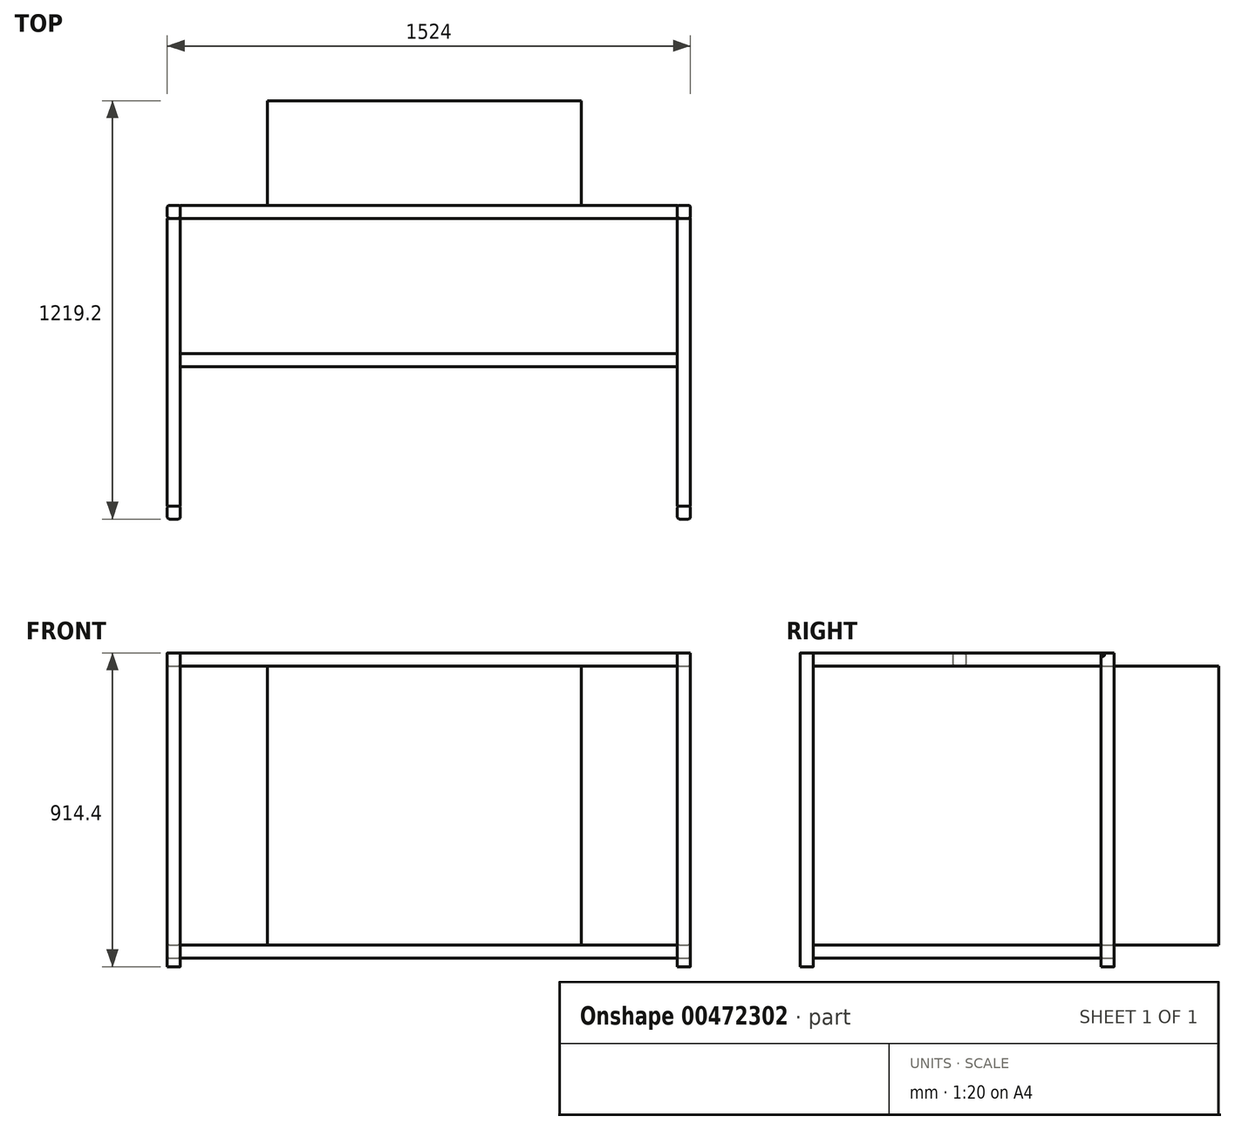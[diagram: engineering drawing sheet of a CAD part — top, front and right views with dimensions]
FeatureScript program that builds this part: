
annotation { "Feature Type Name" : "Feature", "Feature Type Description" : "" }
export const myFeature = defineFeature(function(context is Context, id is Id, definition is map)
    precondition{}
    {
        {
            var Q0;
            Q0=qCreatedBy(makeId("Top.planeOp"),FACE);
            var sketch = newSketch(context, id + "F0", { "sketchPlane" : qUnion([Q0])});
            skLineSegment(sketch, "E0.bottom", {"start": v(-762, 731.56) * mm, "end": v(-723.9, 731.56) * mm});
            skLineSegment(sketch, "E0.top", {"start": v(-762, 693.46) * mm, "end": v(-723.9, 693.46) * mm});
            skLineSegment(sketch, "E0.left", {"start": v(-762, 731.56) * mm, "end": v(-762, 693.46) * mm});
            skLineSegment(sketch, "E0.right", {"start": v(-723.9, 731.56) * mm, "end": v(-723.9, 693.46) * mm});
            skLineSegment(sketch, "E1.bottom", {"start": v(-762, -144.74) * mm, "end": v(-723.9, -144.74) * mm});
            skLineSegment(sketch, "E1.top", {"start": v(-762, -182.84) * mm, "end": v(-723.9, -182.84) * mm});
            skLineSegment(sketch, "E1.left", {"start": v(-762, -144.74) * mm, "end": v(-762, -182.84) * mm});
            skLineSegment(sketch, "E1.right", {"start": v(-723.9, -144.74) * mm, "end": v(-723.9, -182.84) * mm});
            skLineSegment(sketch, "E2.bottom", {"start": v(723.9, -182.84) * mm, "end": v(762, -182.84) * mm});
            skLineSegment(sketch, "E2.top", {"start": v(723.9, -144.74) * mm, "end": v(762, -144.74) * mm});
            skLineSegment(sketch, "E2.left", {"start": v(723.9, -182.84) * mm, "end": v(723.9, -144.74) * mm});
            skLineSegment(sketch, "E2.right", {"start": v(762, -182.84) * mm, "end": v(762, -144.74) * mm});
            skLineSegment(sketch, "E3.bottom", {"start": v(723.9, 731.56) * mm, "end": v(762, 731.56) * mm});
            skLineSegment(sketch, "E3.top", {"start": v(723.9, 693.46) * mm, "end": v(762, 693.46) * mm});
            skLineSegment(sketch, "E3.left", {"start": v(723.9, 731.56) * mm, "end": v(723.9, 693.46) * mm});
            skLineSegment(sketch, "E3.right", {"start": v(762, 731.56) * mm, "end": v(762, 693.46) * mm});
            skSolve(sketch);
        }
        {
            var Q0;
            Q0 = qSketchRegion(id + "F0", true);
            extrude(context, id + "F1", {"entities" : qUnion([Q0]), "depth" : 914.4 * mm});
        }
        {
            var Q0;
            Q0=makeQuery(id+"F1.opExtrude","SWEPT_EDGE",EDGE,{"disambiguationData":[OSD([sQuery(id+"F0.wireOp",EDGE,"E1.top"),sQuery(id+"F0.wireOp",EDGE,"E1.left")])]});
            var Q1;
            Q1=makeQuery(id+"F1.opExtrude","SWEPT_EDGE",EDGE,{"disambiguationData":[OSD([sQuery(id+"F0.wireOp",EDGE,"E1.top"),sQuery(id+"F0.wireOp",EDGE,"E1.right")])]});
            var Q2;
            Q2=makeQuery(id+"F1.opExtrude","SWEPT_EDGE",EDGE,{"disambiguationData":[OSD([sQuery(id+"F0.wireOp",EDGE,"E1.bottom"),sQuery(id+"F0.wireOp",EDGE,"E1.right")])]});
            var Q3;
            Q3=makeQuery(id+"F1.opExtrude","SWEPT_EDGE",EDGE,{"disambiguationData":[OSD([sQuery(id+"F0.wireOp",EDGE,"E0.top"),sQuery(id+"F0.wireOp",EDGE,"E0.left")])]});
            var Q4;
            Q4=makeQuery(id+"F1.opExtrude","SWEPT_EDGE",EDGE,{"disambiguationData":[OSD([sQuery(id+"F0.wireOp",EDGE,"E0.top"),sQuery(id+"F0.wireOp",EDGE,"E0.right")])]});
            var Q5;
            Q5=makeQuery(id+"F1.opExtrude","SWEPT_EDGE",EDGE,{"disambiguationData":[OSD([sQuery(id+"F0.wireOp",EDGE,"E0.bottom"),sQuery(id+"F0.wireOp",EDGE,"E0.right")])]});
            var Q6;
            Q6=makeQuery(id+"F1.opExtrude","SWEPT_EDGE",EDGE,{"disambiguationData":[OSD([sQuery(id+"F0.wireOp",EDGE,"E2.bottom"),sQuery(id+"F0.wireOp",EDGE,"E2.left")])]});
            var Q7;
            Q7=makeQuery(id+"F1.opExtrude","SWEPT_EDGE",EDGE,{"disambiguationData":[OSD([sQuery(id+"F0.wireOp",EDGE,"E2.bottom"),sQuery(id+"F0.wireOp",EDGE,"E2.right")])]});
            var Q8;
            Q8=makeQuery(id+"F1.opExtrude","SWEPT_EDGE",EDGE,{"disambiguationData":[OSD([sQuery(id+"F0.wireOp",EDGE,"E2.top"),sQuery(id+"F0.wireOp",EDGE,"E2.right")])]});
            var Q9;
            Q9=makeQuery(id+"F1.opExtrude","SWEPT_EDGE",EDGE,{"disambiguationData":[OSD([sQuery(id+"F0.wireOp",EDGE,"E3.top"),sQuery(id+"F0.wireOp",EDGE,"E3.left")])]});
            var Q10;
            Q10=makeQuery(id+"F1.opExtrude","SWEPT_EDGE",EDGE,{"disambiguationData":[OSD([sQuery(id+"F0.wireOp",EDGE,"E3.top"),sQuery(id+"F0.wireOp",EDGE,"E3.right")])]});
            var Q11;
            Q11=makeQuery(id+"F1.opExtrude","SWEPT_EDGE",EDGE,{"disambiguationData":[OSD([sQuery(id+"F0.wireOp",EDGE,"E3.bottom"),sQuery(id+"F0.wireOp",EDGE,"E3.right")])]});
            var Q12;
            Q12=makeQuery(id+"F1.opExtrude","SWEPT_EDGE",EDGE,{"disambiguationData":[OSD([sQuery(id+"F0.wireOp",EDGE,"E1.bottom"),sQuery(id+"F0.wireOp",EDGE,"E1.left")])]});
            var Q13;
            Q13=makeQuery(id+"F1.opExtrude","SWEPT_EDGE",EDGE,{"disambiguationData":[OSD([sQuery(id+"F0.wireOp",EDGE,"E2.top"),sQuery(id+"F0.wireOp",EDGE,"E2.left")])]});
            var Q14;
            Q14=makeQuery(id+"F1.opExtrude","SWEPT_EDGE",EDGE,{"disambiguationData":[OSD([sQuery(id+"F0.wireOp",EDGE,"E3.bottom"),sQuery(id+"F0.wireOp",EDGE,"E3.left")])]});
            var Q15;
            Q15=makeQuery(id+"F1.opExtrude","SWEPT_EDGE",EDGE,{"disambiguationData":[OSD([sQuery(id+"F0.wireOp",EDGE,"E0.bottom"),sQuery(id+"F0.wireOp",EDGE,"E0.left")])]});
            fillet(context, id + "F2", {"entities" : qUnion([Q0, Q1, Q2, Q3, Q4, Q5, Q6, Q7, Q8, Q9, Q10, Q11, Q12, Q13, Q14, Q15]), "radius" : 6.35 * mm, "tangentPropagation" : true, "allowEdgeOverflow" : false});
        }
        {
            var Q0;
            Q0=makeQuery(id+"F1.opExtrude","SWEPT_FACE",FACE,{"disambiguationData":[OSD([sQuery(id+"F0.wireOp",EDGE,"E3.right")])]});
            var sketch = newSketch(context, id + "F3", { "sketchPlane" : qUnion([Q0])});
            skLineSegment(sketch, "E4.bottom", {"start": v(-144.74, 914.4) * mm, "end": v(693.46, 914.4) * mm});
            skLineSegment(sketch, "E4.top", {"start": v(-144.74, 876.3) * mm, "end": v(693.46, 876.3) * mm});
            skLineSegment(sketch, "E4.left", {"start": v(-144.74, 914.4) * mm, "end": v(-144.74, 876.3) * mm});
            skLineSegment(sketch, "E4.right", {"start": v(693.46, 914.4) * mm, "end": v(693.46, 876.3) * mm});
            skSolve(sketch);
        }
        {
            var Q0;
            Q0=makeQuery(id+"F3.imprint","IMPRINT",FACE,{"disambiguationData":[TD([[makeQuery(id+"F3.imprint","IMPRINT",EDGE,{"derivedFrom":sQuery(id+"F3.wireOp",EDGE,"E4.bottom")}),-1.0]])]});
            extrude(context, id + "F4", {"entities" : qUnion([Q0]), "oppositeDirection" : true, "depth" : 38.1 * mm});
        }
        {
            var Q0;
            Q0=makeQuery(id+"F4.opExtrude","CAP_EDGE",EDGE,{"disambiguationData":[OSD([sQuery(id+"F3.wireOp",EDGE,"E4.bottom")])],"isStart":true});
            var Q1;
            Q1=makeQuery(id+"F4.opExtrude","CAP_EDGE",EDGE,{"disambiguationData":[OSD([sQuery(id+"F3.wireOp",EDGE,"E4.top")])],"isStart":true});
            var Q2;
            Q2=makeQuery(id+"F4.opExtrude","CAP_EDGE",EDGE,{"disambiguationData":[OSD([sQuery(id+"F3.wireOp",EDGE,"E4.bottom")])],"isStart":false});
            var Q3;
            Q3=makeQuery(id+"F4.opExtrude","CAP_EDGE",EDGE,{"disambiguationData":[OSD([sQuery(id+"F3.wireOp",EDGE,"E4.top")])],"isStart":false});
            fillet(context, id + "F5", {"entities" : qUnion([Q0, Q1, Q2, Q3]), "radius" : 6.35 * mm, "tangentPropagation" : true, "allowEdgeOverflow" : false});
        }
        {
            var Q0;
            Q0=makeQuery(id+"F4.opExtrude","SWEPT_BODY",BODY,{"disambiguationData":[OSD([sQuery(id+"F3.wireOp",EDGE,"E4.bottom"),sQuery(id+"F3.wireOp",EDGE,"E4.top"),sQuery(id+"F3.wireOp",EDGE,"E4.left"),sQuery(id+"F3.wireOp",EDGE,"E4.right")])]});
            transform(context, id + "F6", {"entities" : qUnion([Q0]), "transformType" : TransformType.TRANSLATION_3D, "dx" : -1485.9 * mm, "dy" : 0 * mm, "dz" : 0 * mm, "makeCopy" : true});
        }
        {
            var Q0;
            Q0=makeQuery(id+"F4.opExtrude","SWEPT_BODY",BODY,{"disambiguationData":[OSD([sQuery(id+"F3.wireOp",EDGE,"E4.bottom"),sQuery(id+"F3.wireOp",EDGE,"E4.top"),sQuery(id+"F3.wireOp",EDGE,"E4.left"),sQuery(id+"F3.wireOp",EDGE,"E4.right")])]});
            transform(context, id + "F7", {"entities" : qUnion([Q0]), "transformType" : TransformType.TRANSLATION_3D, "dx" : 0 * mm, "dy" : 0 * mm, "dz" : -850.9 * mm, "makeCopy" : true});
        }
        {
            var Q0;
            Q0=makeQuery(id+"F7.opPattern","COPY",BODY,{"derivedFrom":makeQuery(id+"F4.opExtrude","SWEPT_BODY",BODY,{"disambiguationData":[OSD([sQuery(id+"F3.wireOp",EDGE,"E4.bottom"),sQuery(id+"F3.wireOp",EDGE,"E4.top"),sQuery(id+"F3.wireOp",EDGE,"E4.left"),sQuery(id+"F3.wireOp",EDGE,"E4.right")])]}),"instanceName":"1"});
            transform(context, id + "F8", {"entities" : qUnion([Q0]), "transformType" : TransformType.TRANSLATION_3D, "dx" : -1485.9 * mm, "dy" : 0 * mm, "dz" : 0 * mm, "makeCopy" : true});
        }
        {
            var Q0;
            Q0=makeQuery(id+"F1.opExtrude","SWEPT_FACE",FACE,{"disambiguationData":[OSD([sQuery(id+"F0.wireOp",EDGE,"E3.bottom")])]});
            var sketch = newSketch(context, id + "F9", { "sketchPlane" : qUnion([Q0])});
            skLineSegment(sketch, "E5.bottom", {"start": v(-723.9, 914.4) * mm, "end": v(723.9, 914.4) * mm});
            skLineSegment(sketch, "E5.top", {"start": v(-723.9, 876.3) * mm, "end": v(723.9, 876.3) * mm});
            skLineSegment(sketch, "E5.left", {"start": v(-723.9, 914.4) * mm, "end": v(-723.9, 876.3) * mm});
            skLineSegment(sketch, "E5.right", {"start": v(723.9, 914.4) * mm, "end": v(723.9, 876.3) * mm});
            skSolve(sketch);
        }
        {
            var Q0;
            Q0 = qSketchRegion(id + "F9", true);
            extrude(context, id + "F10", {"entities" : qUnion([Q0]), "oppositeDirection" : true, "depth" : 38.1 * mm});
        }
        {
            var Q0;
            Q0=makeQuery(id+"F10.opExtrude","CAP_EDGE",EDGE,{"disambiguationData":[OSD([sQuery(id+"F9.wireOp",EDGE,"E5.bottom")])],"isStart":true});
            var Q1;
            Q1=makeQuery(id+"F10.opExtrude","CAP_EDGE",EDGE,{"disambiguationData":[OSD([sQuery(id+"F9.wireOp",EDGE,"E5.bottom")])],"isStart":false});
            var Q2;
            Q2=makeQuery(id+"F10.opExtrude","CAP_EDGE",EDGE,{"disambiguationData":[OSD([sQuery(id+"F9.wireOp",EDGE,"E5.top")])],"isStart":true});
            var Q3;
            Q3=makeQuery(id+"F10.opExtrude","CAP_EDGE",EDGE,{"disambiguationData":[OSD([sQuery(id+"F9.wireOp",EDGE,"E5.top")])],"isStart":false});
            fillet(context, id + "F11", {"entities" : qUnion([Q0, Q1, Q2, Q3]), "radius" : 5.08 * mm, "tangentPropagation" : true, "allowEdgeOverflow" : false});
        }
        {
            var Q0;
            Q0=makeQuery(id+"F10.opExtrude","SWEPT_BODY",BODY,{"disambiguationData":[OSD([sQuery(id+"F9.wireOp",EDGE,"E5.bottom"),sQuery(id+"F9.wireOp",EDGE,"E5.top"),sQuery(id+"F9.wireOp",EDGE,"E5.left"),sQuery(id+"F9.wireOp",EDGE,"E5.right")])]});
            transform(context, id + "F12", {"entities" : qUnion([Q0]), "transformType" : TransformType.TRANSLATION_3D, "dx" : 0 * mm, "dy" : 0 * mm, "dz" : -850.9 * mm, "makeCopy" : true});
        }
        {
            var Q0;
            Q0=makeQuery(id+"F10.opExtrude","SWEPT_BODY",BODY,{"disambiguationData":[OSD([sQuery(id+"F9.wireOp",EDGE,"E5.bottom"),sQuery(id+"F9.wireOp",EDGE,"E5.top"),sQuery(id+"F9.wireOp",EDGE,"E5.left"),sQuery(id+"F9.wireOp",EDGE,"E5.right")])]});
            transform(context, id + "F13", {"entities" : qUnion([Q0]), "transformType" : TransformType.TRANSLATION_3D, "dx" : 0 * mm, "dy" : -431.8 * mm, "dz" : 0 * mm, "makeCopy" : true});
        }
        {
            var Q0;
            Q0=makeQuery(id+"F1.opExtrude","SWEPT_FACE",FACE,{"disambiguationData":[OSD([sQuery(id+"F0.wireOp",EDGE,"E0.left")])]});
            var sketch = newSketch(context, id + "F14", { "sketchPlane" : qUnion([Q0])});
            skLineSegment(sketch, "E6.bottom", {"start": v(-731.56, 876.3) * mm, "end": v(-1036.36, 876.3) * mm});
            skLineSegment(sketch, "E6.top", {"start": v(-731.56, 63.5) * mm, "end": v(-1036.36, 63.5) * mm});
            skLineSegment(sketch, "E6.left", {"start": v(-731.56, 876.3) * mm, "end": v(-731.56, 63.5) * mm});
            skLineSegment(sketch, "E6.right", {"start": v(-1036.36, 876.3) * mm, "end": v(-1036.36, 63.5) * mm});
            skSolve(sketch);
        }
        {
            var Q0;
            Q0 = qSketchRegion(id + "F14", true);
            extrude(context, id + "F15", {"entities" : qUnion([Q0]), "oppositeDirection" : true, "depth" : 914.4 * mm});
        }
        {
            var Q0;
            Q0=makeQuery(id+"F15.opExtrude","SWEPT_BODY",BODY,{"disambiguationData":[OSD([sQuery(id+"F14.wireOp",EDGE,"E6.bottom"),sQuery(id+"F14.wireOp",EDGE,"E6.top"),sQuery(id+"F14.wireOp",EDGE,"E6.left"),sQuery(id+"F14.wireOp",EDGE,"E6.right")])]});
            transform(context, id + "F16", {"entities" : qUnion([Q0]), "transformType" : TransformType.TRANSLATION_3D, "dx" : 292.1 * mm, "dy" : 0 * mm, "dz" : 0 * mm, "makeCopy" : false});
        }
    });
